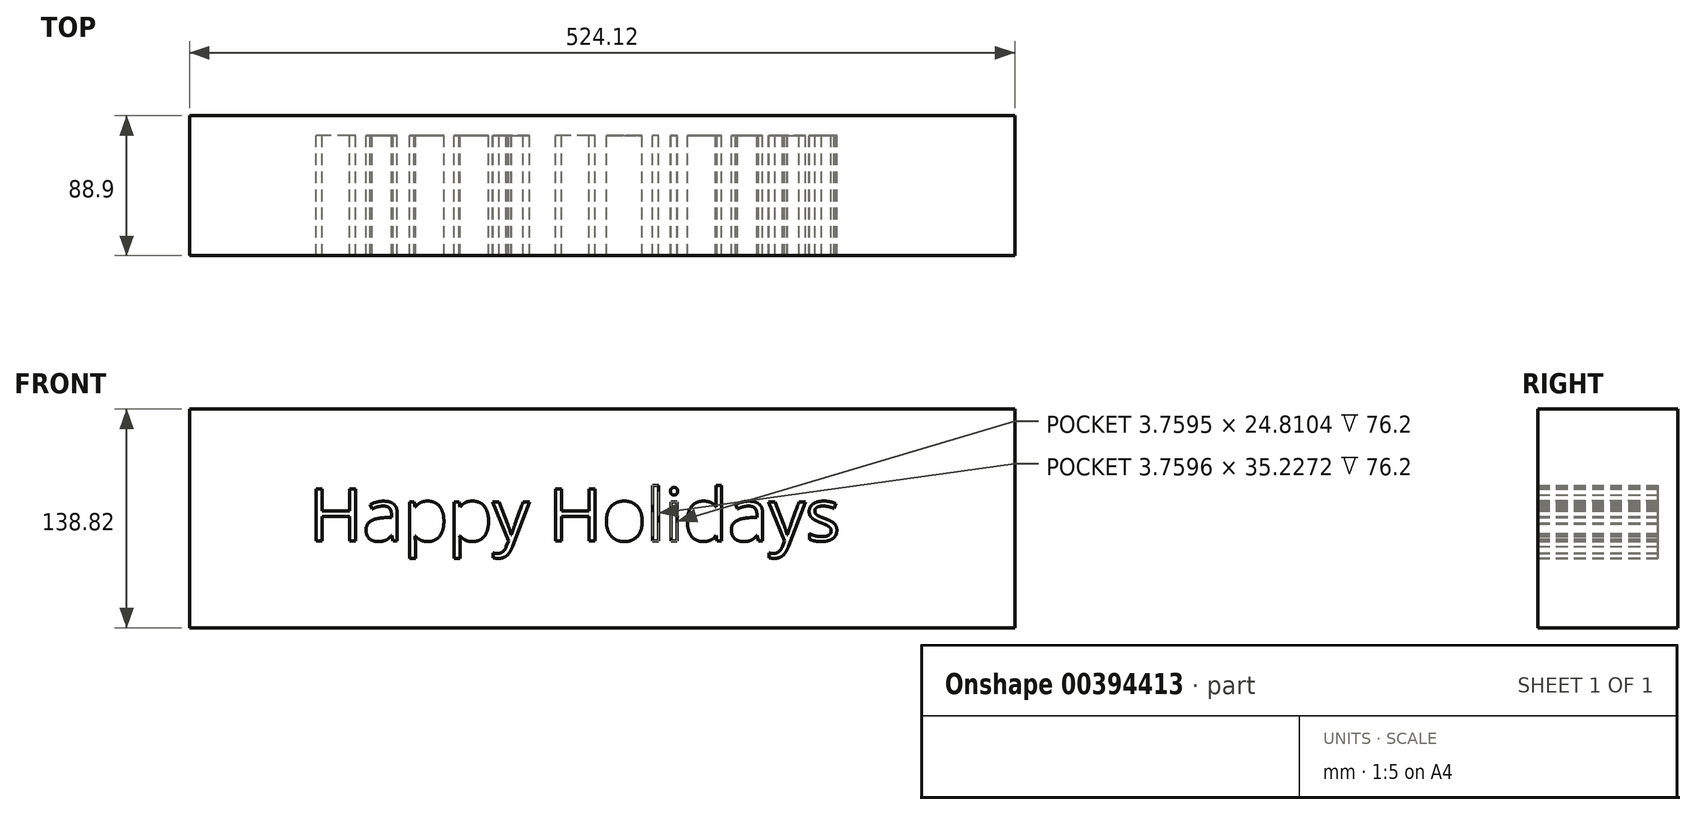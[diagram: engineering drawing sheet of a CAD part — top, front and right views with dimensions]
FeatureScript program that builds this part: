
annotation { "Feature Type Name" : "Feature", "Feature Type Description" : "" }
export const myFeature = defineFeature(function(context is Context, id is Id, definition is map)
    precondition{}
    {
        {
            var Q0;
            Q0=qCreatedBy(makeId("Front.planeOp"),FACE);
            var sketch = newSketch(context, id + "F0", { "sketchPlane" : qUnion([Q0])});
            skLineSegment(sketch, "E0.bottom", {"start": v(-262.06, 69.4) * mm, "end": v(262.06, 69.4) * mm});
            skLineSegment(sketch, "E0.top", {"start": v(-262.06, -69.4) * mm, "end": v(262.06, -69.4) * mm});
            skLineSegment(sketch, "E0.left", {"start": v(-262.06, 69.4) * mm, "end": v(-262.06, -69.4) * mm});
            skLineSegment(sketch, "E0.right", {"start": v(262.06, 69.4) * mm, "end": v(262.06, -69.4) * mm});
            skPoint(sketch, "E0.middle", {"position": v(0, 0) * mm});
            skSolve(sketch);
        }
        {
            var Q0;
            Q0=makeQuery(id+"F0.imprint","IMPRINT",FACE,{"disambiguationData":[TD([[makeQuery(id+"F0.imprint","IMPRINT",EDGE,{"derivedFrom":sQuery(id+"F0.wireOp",EDGE,"E0.bottom")}),-1.0]])]});
            extrude(context, id + "F1", {"entities" : qUnion([Q0]), "depth" : 12.7 * mm});
        }
        {
            var Q0;
            Q0=makeQuery(id+"F1.opExtrude","CAP_FACE",FACE,{"disambiguationData":[OSD([sQuery(id+"F0.wireOp",EDGE,"E0.bottom"),sQuery(id+"F0.wireOp",EDGE,"E0.top"),sQuery(id+"F0.wireOp",EDGE,"E0.left"),sQuery(id+"F0.wireOp",EDGE,"E0.right")])],"isStart":false});
            var sketch = newSketch(context, id + "F2", { "sketchPlane" : qUnion([Q0])});
            skText(sketch, "E1", { "text": "Happy Holidays", "fontName": "OpenSans-Regular.ttf"});
            const initialGuessF2  = {"E1": [-0.18639, -0.01421, 1, 0, 0.03338]};
            skSetInitialGuess(sketch, initialGuessF2);
            skSolve(sketch);
        }
        {
            var Q0;
            Q0=makeQuery(id+"F2.imprint","IMPRINT",FACE,{"disambiguationData":[TD([[makeQuery(id+"F2.imprint","IMPRINT",EDGE,{"derivedFrom":sQuery(id+"F2.wireOp",EDGE,"E1.sketch_text.stroke-89")}),1.0]])]});
            extrude(context, id + "F3", {"entities" : qUnion([Q0]), "operationType" : NewBodyOperationType.ADD, "depth" : 76.2 * mm});
        }
    });
